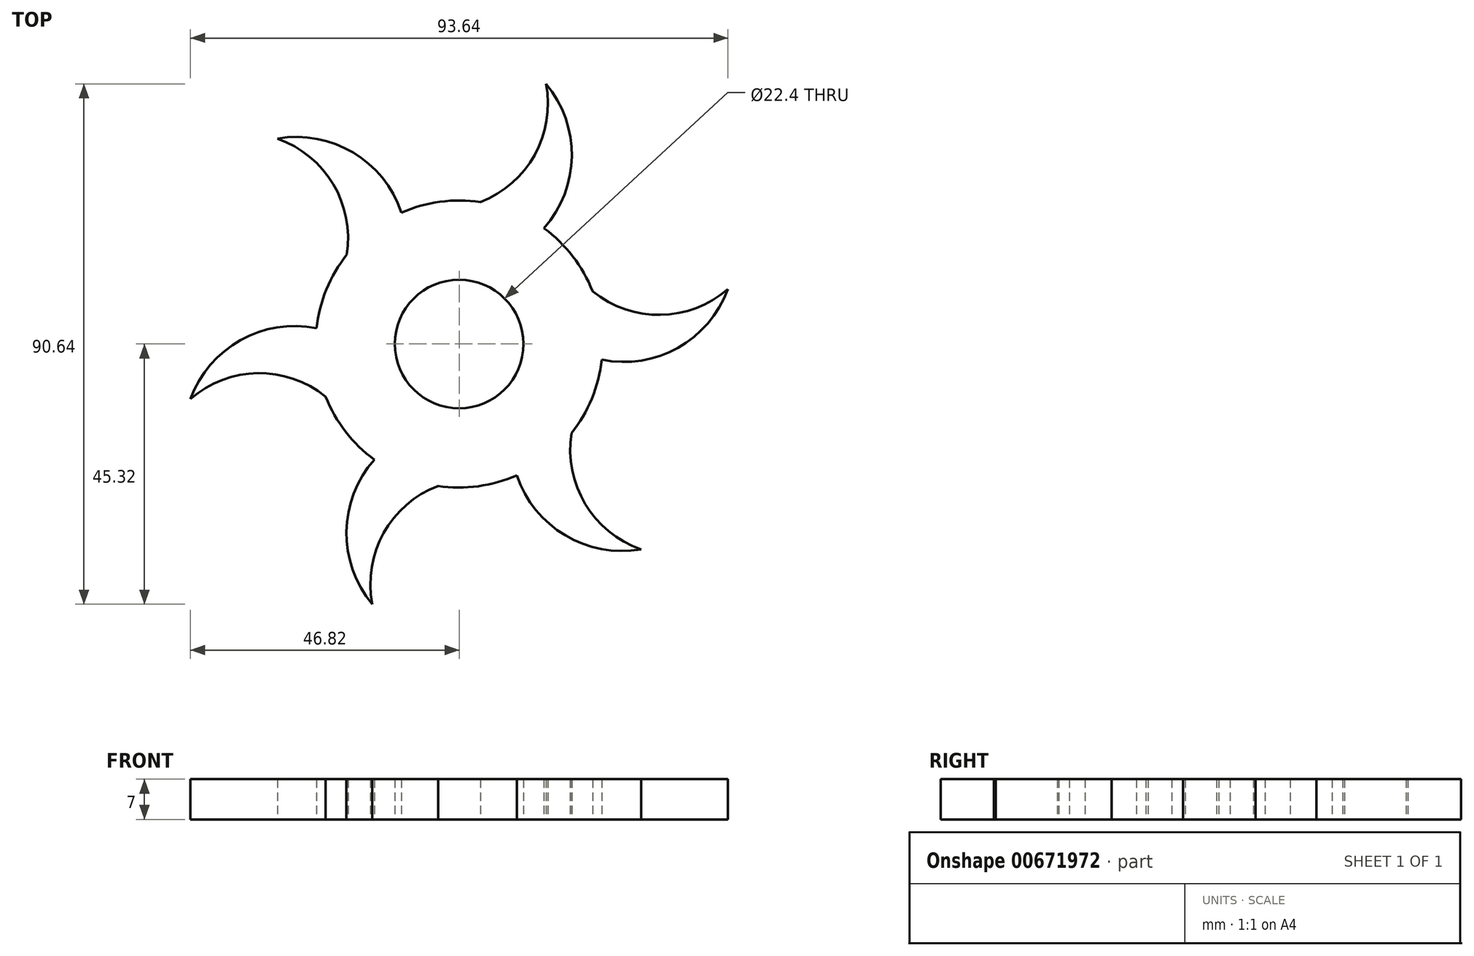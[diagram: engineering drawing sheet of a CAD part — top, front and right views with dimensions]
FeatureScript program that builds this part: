
annotation { "Feature Type Name" : "Feature", "Feature Type Description" : "" }
export const myFeature = defineFeature(function(context is Context, id is Id, definition is map)
    precondition{}
    {
        {
            var Q0;
            Q0=qCreatedBy(makeId("Top.planeOp"),FACE);
            var sketch = newSketch(context, id + "F0", { "sketchPlane" : qUnion([Q0])});
            skCircle(sketch, "E0", {"center": v(0, 0) * mm, "radius": 11.2 * mm});
            skCircle(sketch, "E1", {"center": v(0, 0) * mm, "radius": 25 * mm});
            skArc(sketch, "E2", {"start": v(-10.06, 22.89) * mm, "mid": v(-18.48, 33.34) * mm, "end": v(-31.68, 35.77) * mm});
            skArc(sketch, "E3", {"start": v(-19.58, 15.55) * mm, "mid": v(-21.96, 27.86) * mm, "end": v(-31.68, 35.77) * mm});
            skArc(sketch, "E4.1.0", {"start": v(-24.85, 2.73) * mm, "mid": v(-38.11, 0.67) * mm, "end": v(-46.82, -9.55) * mm});
            skArc(sketch, "E4.1.1", {"start": v(-23.25, -9.18) * mm, "mid": v(-35.1, -5.08) * mm, "end": v(-46.82, -9.55) * mm});
            skArc(sketch, "E4.2.0", {"start": v(-14.8, -20.16) * mm, "mid": v(-19.63, -32.68) * mm, "end": v(-15.14, -45.32) * mm});
            skArc(sketch, "E4.2.1", {"start": v(-3.68, -24.73) * mm, "mid": v(-13.15, -32.94) * mm, "end": v(-15.14, -45.32) * mm});
            skArc(sketch, "E4.3.0", {"start": v(10.06, -22.89) * mm, "mid": v(18.48, -33.34) * mm, "end": v(31.68, -35.77) * mm});
            skArc(sketch, "E4.3.1", {"start": v(19.58, -15.55) * mm, "mid": v(21.96, -27.86) * mm, "end": v(31.68, -35.77) * mm});
            skArc(sketch, "E4.4.0", {"start": v(24.85, -2.73) * mm, "mid": v(38.11, -0.67) * mm, "end": v(46.82, 9.55) * mm});
            skArc(sketch, "E4.4.1", {"start": v(23.25, 9.18) * mm, "mid": v(35.1, 5.08) * mm, "end": v(46.82, 9.55) * mm});
            skArc(sketch, "E4.5.0", {"start": v(14.8, 20.16) * mm, "mid": v(19.63, 32.68) * mm, "end": v(15.14, 45.32) * mm});
            skArc(sketch, "E4.5.1", {"start": v(3.68, 24.73) * mm, "mid": v(13.15, 32.94) * mm, "end": v(15.14, 45.32) * mm});
            skLineSegment(sketch, "E5", {"start": v(-19.58, 15.55) * mm, "end": v(-10.15, 4.74) * mm});
            skLineSegment(sketch, "E6", {"start": v(-10.15, 4.74) * mm, "end": v(-24.85, 2.73) * mm});
            skLineSegment(sketch, "E7.1.0", {"start": v(-23.25, -9.18) * mm, "end": v(-9.18, -6.42) * mm});
            skLineSegment(sketch, "E7.1.1", {"start": v(-9.18, -6.42) * mm, "end": v(-14.8, -20.16) * mm});
            skLineSegment(sketch, "E7.2.0", {"start": v(-3.68, -24.73) * mm, "end": v(0.97, -11.16) * mm});
            skLineSegment(sketch, "E7.2.1", {"start": v(0.97, -11.16) * mm, "end": v(10.06, -22.89) * mm});
            skLineSegment(sketch, "E7.3.0", {"start": v(19.58, -15.55) * mm, "end": v(10.15, -4.74) * mm});
            skLineSegment(sketch, "E7.3.1", {"start": v(10.15, -4.74) * mm, "end": v(24.85, -2.73) * mm});
            skLineSegment(sketch, "E7.4.0", {"start": v(23.25, 9.18) * mm, "end": v(9.18, 6.42) * mm});
            skLineSegment(sketch, "E7.4.1", {"start": v(9.18, 6.42) * mm, "end": v(14.8, 20.16) * mm});
            skLineSegment(sketch, "E7.5.0", {"start": v(3.68, 24.73) * mm, "end": v(-0.97, 11.16) * mm});
            skLineSegment(sketch, "E7.5.1", {"start": v(-0.97, 11.16) * mm, "end": v(-10.06, 22.89) * mm});
            skSolve(sketch);
        }
        {
            var Q0;
            {var subQ0=sQuery(id+"F0.wireOp",EDGE,"E4.2.0");Q0=makeQuery(id+"F0.imprint","IMPRINT",FACE,{"disambiguationData":[TD([[makeQuery(id+"F0.imprint","IMPRINT",EDGE,{"derivedFrom":subQ0}),1.0]])]});}
            var Q1;
            {var subQ0=sQuery(id+"F0.wireOp",EDGE,"E7.3.1");Q1=makeQuery(id+"F0.imprint","IMPRINT",FACE,{"disambiguationData":[TD([[makeQuery(id+"F0.imprint","IMPRINT",EDGE,{"derivedFrom":subQ0}),1.0]])]});}
            var Q2;
            {var subQ0=sQuery(id+"F0.wireOp",EDGE,"E7.4.1");Q2=makeQuery(id+"F0.imprint","IMPRINT",FACE,{"disambiguationData":[TD([[makeQuery(id+"F0.imprint","IMPRINT",EDGE,{"derivedFrom":subQ0}),1.0]])]});}
            var Q3;
            {var subQ0=sQuery(id+"F0.wireOp",EDGE,"E5");Q3=makeQuery(id+"F0.imprint","IMPRINT",FACE,{"disambiguationData":[TD([[makeQuery(id+"F0.imprint","IMPRINT",EDGE,{"derivedFrom":subQ0}),1.0]])]});}
            var Q4;
            {var subQ0=sQuery(id+"F0.wireOp",EDGE,"E6");Q4=makeQuery(id+"F0.imprint","IMPRINT",FACE,{"disambiguationData":[TD([[makeQuery(id+"F0.imprint","IMPRINT",EDGE,{"derivedFrom":subQ0}),1.0]])]});}
            var Q5;
            {var subQ0=sQuery(id+"F0.wireOp",EDGE,"E4.1.0");Q5=makeQuery(id+"F0.imprint","IMPRINT",FACE,{"disambiguationData":[TD([[makeQuery(id+"F0.imprint","IMPRINT",EDGE,{"derivedFrom":subQ0}),1.0]])]});}
            var Q6;
            {var subQ0=sQuery(id+"F0.wireOp",EDGE,"E2");Q6=makeQuery(id+"F0.imprint","IMPRINT",FACE,{"disambiguationData":[TD([[makeQuery(id+"F0.imprint","IMPRINT",EDGE,{"derivedFrom":subQ0}),1.0]])]});}
            var Q7;
            {var subQ0=sQuery(id+"F0.wireOp",EDGE,"E4.5.0");Q7=makeQuery(id+"F0.imprint","IMPRINT",FACE,{"disambiguationData":[TD([[makeQuery(id+"F0.imprint","IMPRINT",EDGE,{"derivedFrom":subQ0}),1.0]])]});}
            var Q8;
            {var subQ0=sQuery(id+"F0.wireOp",EDGE,"E4.4.0");Q8=makeQuery(id+"F0.imprint","IMPRINT",FACE,{"disambiguationData":[TD([[makeQuery(id+"F0.imprint","IMPRINT",EDGE,{"derivedFrom":subQ0}),1.0]])]});}
            var Q9;
            {var subQ0=sQuery(id+"F0.wireOp",EDGE,"E7.2.1");Q9=makeQuery(id+"F0.imprint","IMPRINT",FACE,{"disambiguationData":[TD([[makeQuery(id+"F0.imprint","IMPRINT",EDGE,{"derivedFrom":subQ0}),1.0]])]});}
            var Q10;
            {var subQ0=sQuery(id+"F0.wireOp",EDGE,"E7.1.1");Q10=makeQuery(id+"F0.imprint","IMPRINT",FACE,{"disambiguationData":[TD([[makeQuery(id+"F0.imprint","IMPRINT",EDGE,{"derivedFrom":subQ0}),1.0]])]});}
            var Q11;
            {var subQ0=sQuery(id+"F0.wireOp",EDGE,"E4.3.0");Q11=makeQuery(id+"F0.imprint","IMPRINT",FACE,{"disambiguationData":[TD([[makeQuery(id+"F0.imprint","IMPRINT",EDGE,{"derivedFrom":subQ0}),1.0]])]});}
            var Q12;
            {var subQ0=sQuery(id+"F0.wireOp",EDGE,"E7.3.0");Q12=makeQuery(id+"F0.imprint","IMPRINT",FACE,{"disambiguationData":[TD([[makeQuery(id+"F0.imprint","IMPRINT",EDGE,{"derivedFrom":subQ0}),-1.0]])]});}
            var Q13;
            {var subQ0=sQuery(id+"F0.wireOp",EDGE,"E7.2.0");Q13=makeQuery(id+"F0.imprint","IMPRINT",FACE,{"disambiguationData":[TD([[makeQuery(id+"F0.imprint","IMPRINT",EDGE,{"derivedFrom":subQ0}),-1.0]])]});}
            var Q14;
            {var subQ0=sQuery(id+"F0.wireOp",EDGE,"E7.1.0");Q14=makeQuery(id+"F0.imprint","IMPRINT",FACE,{"disambiguationData":[TD([[makeQuery(id+"F0.imprint","IMPRINT",EDGE,{"derivedFrom":subQ0}),-1.0]])]});}
            var Q15;
            {var subQ0=sQuery(id+"F0.wireOp",EDGE,"E5");Q15=makeQuery(id+"F0.imprint","IMPRINT",FACE,{"disambiguationData":[TD([[makeQuery(id+"F0.imprint","IMPRINT",EDGE,{"derivedFrom":subQ0}),-1.0]])]});}
            var Q16;
            {var subQ0=sQuery(id+"F0.wireOp",EDGE,"E7.4.0");Q16=makeQuery(id+"F0.imprint","IMPRINT",FACE,{"disambiguationData":[TD([[makeQuery(id+"F0.imprint","IMPRINT",EDGE,{"derivedFrom":subQ0}),-1.0]])]});}
            var Q17;
            {var subQ2=sQuery(id+"F0.wireOp",EDGE,"E7.5.0");Q17=makeQuery(id+"F0.imprint","IMPRINT",FACE,{"disambiguationData":[TD([[makeQuery(id+"F0.imprint","IMPRINT",EDGE,{"derivedFrom":subQ2}),-1.0]])]});}
            extrude(context, id + "F1", {"entities" : qUnion([Q0, Q1, Q2, Q3, Q4, Q5, Q6, Q7, Q8, Q9, Q10, Q11, Q12, Q13, Q14, Q15, Q16, Q17]), "depth" : 7 * mm, "offsetDistance" : 25 * mm});
        }
    });
